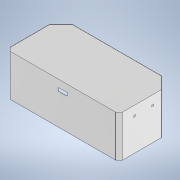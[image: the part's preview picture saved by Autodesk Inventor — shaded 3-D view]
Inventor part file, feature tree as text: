
AUTODESK INVENTOR PART (.ipt)
format: ipt  version: 2022.1 (Build 261234000, 234)  size: 395,264 bytes
history: native  units: mm
features: reference x16, sketch x11, extrude x10, other x8, hole x2, projected_geometry x2, plane x1
ambient origin geometry x8: Origin, YZ Plane, XZ Plane, XY Plane, X Axis, Y Axis, Z Axis, Center Point
bodies: Body1 (feature_tree)
feature tree (50):
  other  "Sólido1"
  plane  "Plano de trabajo1"
  extrude  "Extrusión1"  Depth=1.5mm TaperAngle=0.0deg
  extrude  "Extrusión2"  Depth=10.0mm
  hole  "Agujero1"  [1 undecoded]
  extrude  "Extrusión3"  Depth=10.0mm
  hole  "Agujero2"  [1 undecoded]
  extrude  "Extrusión6"  Depth=100.0mm
  extrude  "Extrusión7"  Depth=5.5mm
  extrude  "Extrusión8"  Depth=10.0mm TaperAngle=0.0deg
  extrude  "Extrusión9"  Depth=7.5mm
  extrude  "Extrusión10"  Depth=5.5mm
  extrude  "Extrusión11"  Depth=5.5mm
  extrude  "Extrusión12"  Depth=10.0mm TaperAngle=0.0deg
  reference  "Referencia1"
  reference  "Referencia2"
  reference  "Referencia3"
  reference  "Referencia4"
  reference  "Referencia5"
  reference  "Referencia6"
  reference  "Referencia7"
  reference  "Referencia8"
  sketch  "Boceto2"  dims[d1=400.0mm d2=0.0mm d3=1.5mm d4=0.0mm]
  projected_geometry  "Contorno proyectado1"
  sketch  "Boceto4"  dims[d5=10.0mm d6=10.0mm]
  reference  "Referencia9"
  sketch  "Boceto6"  dims[d7=5.0mm d8=200.0mm]
  sketch  "Boceto7"  dims[d9=200.0mm]
  reference  "Referencia10"
  sketch  "Boceto11"  dims[d10=3.4mm d11=10.0mm d12=10.4mm d13=2.0mm d14=90.0deg d15=6.0mm d16=20.594885mm d17=7.5mm]
  sketch  "Boceto12"  dims[d19=15.0mm d20=0.0mm d21=5.0mm]
  sketch  "Boceto13"  dims[d23=100.0mm d24=100.0mm]
  sketch  "Boceto14"  dims[d26=3.4mm d27=10.0mm d28=4.0mm d29=2.0mm d30=90.0deg d31=8.0mm d32=20.594885mm d39=5.5mm]
  sketch  "Boceto15"  dims[d40=5.5mm d41=10.0mm d42=0.0mm]
  reference  "Referencia11"
  reference  "Referencia12"
  reference  "Referencia13"
  reference  "Referencia14"
  reference  "Referencia15"
  reference  "Referencia16"
  projected_geometry  "Contorno proyectado4"
  sketch  "Boceto16"  dims[d43=7.5mm d44=7.5mm]
  sketch  "Boceto17"  dims[d45=15.0mm d46=0.0mm d47=5.5mm d48=5.5mm d49=10.0mm d50=0.0mm d51=7.5mm d52=7.5mm d53=15.0mm d54=0.0mm d55=5.5mm d56=5.5mm d57=10.0mm d58=0.0mm d60=10.0mm d62=10.0mm d63=1.5mm d65=80.0mm d67=1.5mm d68=0.0mm d69=80.0mm d70=80.0mm d71=70.0mm d72=30.0mm d73=90.0mm d74=1.5mm d75=0.0mm d76=5.0mm d77=5.0mm d78=5.0mm d79=5.0mm]
  other  "<userpath>\Desktop\PDM\ProyectoRobotPallet\RobotPallet.iam"
  other  "RobotPallet.iam"
  other  "CubieraInferior:1"
  other  "EstructuraInferior:1"
  other  "Frame_Base:1"
  other  "ISO 10799-2 40x40x2 - 2899.41:1"
  other  "ISO 10799-2 40x40x2 - 325.18:3"
note: 2 required parameter values undecoded (feature->parameter linkage not recoverable at this tier; creation-order binding heuristic only, values carry confidence <= 0.55)
